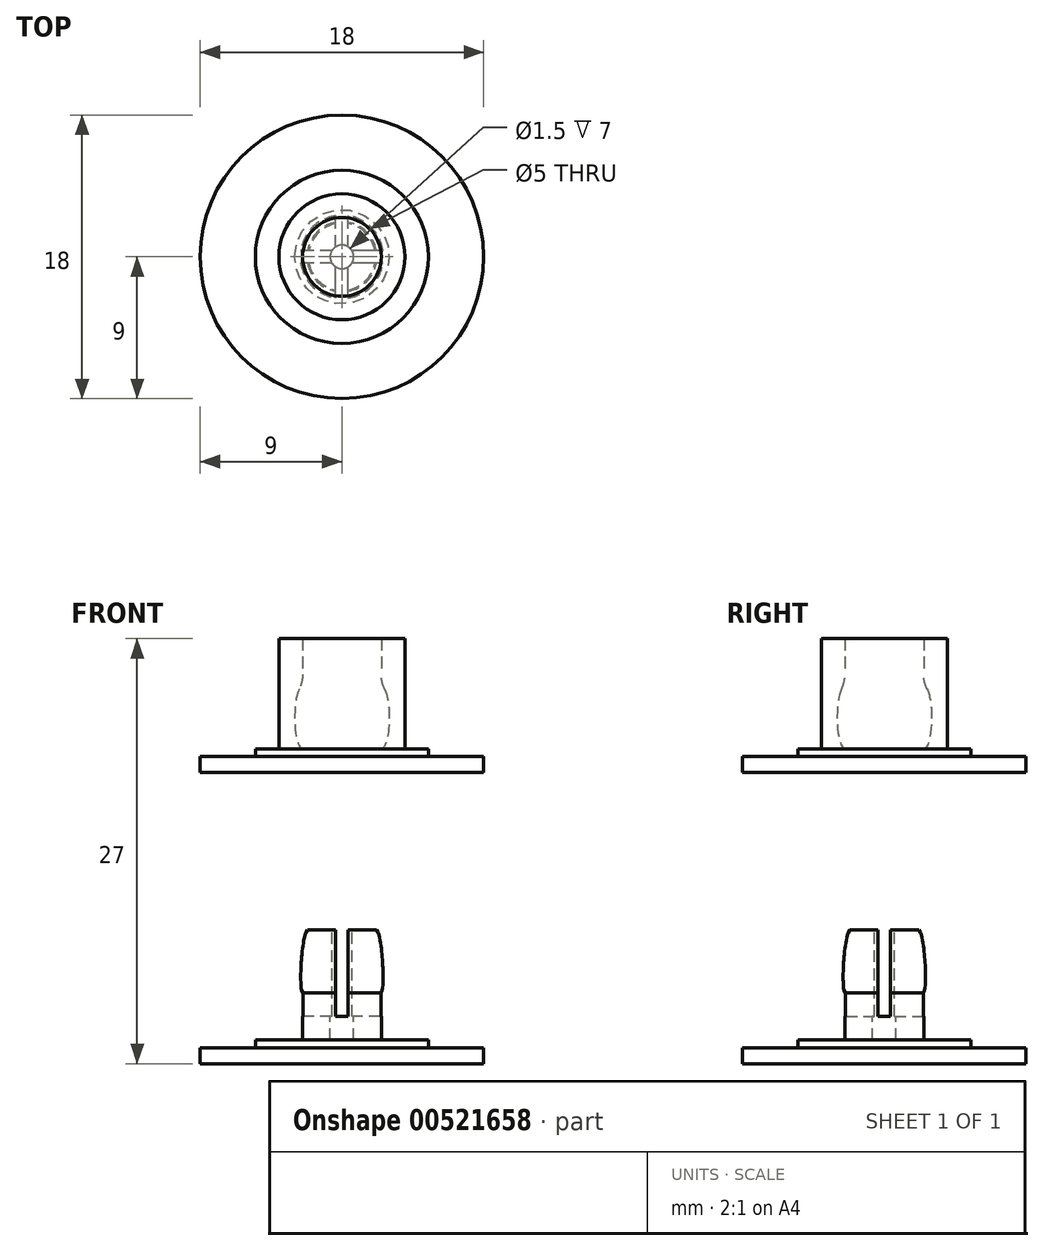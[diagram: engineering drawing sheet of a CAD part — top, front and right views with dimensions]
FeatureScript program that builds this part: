
annotation { "Feature Type Name" : "Feature", "Feature Type Description" : "" }
export const myFeature = defineFeature(function(context is Context, id is Id, definition is map)
    precondition{}
    {
        {
            var Q0;
            Q0=qCreatedBy(makeId("Front.planeOp"),FACE);
            var sketch = newSketch(context, id + "F0", { "sketchPlane" : qUnion([Q0])});
            skLineSegment(sketch, "E0", {"start": v(0, 0) * mm, "end": v(-9, 0) * mm});
            skLineSegment(sketch, "E1", {"start": v(-9, 0) * mm, "end": v(-9, 1) * mm});
            skLineSegment(sketch, "E2", {"start": v(-9, 1) * mm, "end": v(-5.5, 1) * mm});
            skLineSegment(sketch, "E3", {"start": v(-5.5, 1) * mm, "end": v(-5.5, 1.5) * mm});
            skLineSegment(sketch, "E4", {"start": v(-4, 1.5) * mm, "end": v(-5.5, 1.5) * mm});
            skLineSegment(sketch, "E5", {"start": v(-4, 1.5) * mm, "end": v(-4, 8.5) * mm});
            skLineSegment(sketch, "E6", {"start": v(-4, 8.5) * mm, "end": v(-2.5, 8.5) * mm});
            skLineSegment(sketch, "E7", {"start": v(0, -18.5) * mm, "end": v(-9, -18.5) * mm});
            skLineSegment(sketch, "E8", {"start": v(-9, -18.5) * mm, "end": v(-9, -17.5) * mm});
            skLineSegment(sketch, "E9", {"start": v(-9, -17.5) * mm, "end": v(-5.5, -17.5) * mm});
            skLineSegment(sketch, "E10", {"start": v(-5.5, -17.5) * mm, "end": v(-5.5, -17) * mm});
            skLineSegment(sketch, "E11", {"start": v(-5.5, -17) * mm, "end": v(-4, -17) * mm});
            skLineSegment(sketch, "E12", {"start": v(-2.5, -15) * mm, "end": v(-2.5, -14) * mm});
            skLineSegment(sketch, "E13", {"start": v(-2.5, 8.5) * mm, "end": v(-2.5, 5.5) * mm});
            skLineSegment(sketch, "E14", {"start": v(-2.5, 1.5) * mm, "end": v(0, 1.5) * mm});
            skLineSegment(sketch, "E15", {"start": v(0, 0) * mm, "end": v(0, 1.5) * mm});
            skEllipticalArc(sketch, "E16", {});
            skEllipticalArc(sketch, "E17", {});
            skLineSegment(sketch, "E18", {"start": v(0, -17) * mm, "end": v(-0.75, -17) * mm});
            skLineSegment(sketch, "E19", {"start": v(-0.75, -17) * mm, "end": v(-0.75, -10) * mm});
            skLineSegment(sketch, "E20", {"start": v(0, -17) * mm, "end": v(0, -18.5) * mm});
            skLineSegment(sketch, "E21", {"start": v(-2.5, -15) * mm, "end": v(-2.5, -17) * mm});
            skLineSegment(sketch, "E22", {"start": v(-4, -17) * mm, "end": v(-2.5, -17) * mm});
            skLineSegment(sketch, "E23", {"start": v(-0.75, -10) * mm, "end": v(-2.14, -10) * mm});
            skLineSegment(sketch, "E24", {"start": v(-2.14, -10) * mm, "end": v(-2.22, -10) * mm});
            const initialGuessF0  = {"E16": [-0.0023604902154368427, -0.012004871899480357, -0.06975647374412519, -0.9975640502598243, 0.002, 0.00025, 3.1415926535897936, 0], "E17": [-0.0025, 0.0035, 0, -1, 0.002, 0.0005, 3.1415926535897936, 0]};
            skSetInitialGuess(sketch, initialGuessF0);
            skSolve(sketch);
        }
        {
            var Q0;
            Q0=makeQuery(id+"F0.imprint","IMPRINT",FACE,{"disambiguationData":[TD([[makeQuery(id+"F0.imprint","IMPRINT",EDGE,{"derivedFrom":sQuery(id+"F0.wireOp",EDGE,"E0")}),-1.0]])]});
            var Q1;
            Q1=sQuery(id+"F0.wireOp",EDGE,"E15");
            revolve(context, id + "F1", {"entities" : qUnion([Q0]), "axis" : qUnion([Q1]), "revolveType" : RevolveType.ONE_DIRECTION, "angle" : 360 * degree});
        }
        {
            var Q0;
            Q0=makeQuery(id+"F1.opRevolve","SWEPT_EDGE",EDGE,{"disambiguationData":[OSD([sQuery(id+"F0.wireOp",EDGE,"E13"),sQuery(id+"F0.wireOp",EDGE,"E17")])]});
            fillet(context, id + "F2", {"entities" : qUnion([Q0]), "radius" : 2 * mm, "tangentPropagation" : true, "allowEdgeOverflow" : false});
        }
        {
            var Q0;
            Q0=makeQuery(id+"F0.imprint","IMPRINT",FACE,{"disambiguationData":[TD([[makeQuery(id+"F0.imprint","IMPRINT",EDGE,{"derivedFrom":sQuery(id+"F0.wireOp",EDGE,"E7")}),-1.0]])]});
            var Q1;
            Q1=sQuery(id+"F0.wireOp",EDGE,"E20");
            revolve(context, id + "F3", {"entities" : qUnion([Q0]), "axis" : qUnion([Q1]), "revolveType" : RevolveType.FULL});
        }
        {
            var Q0;
            Q0=makeQuery(id+"F3.opRevolve","SWEPT_FACE",FACE,{"disambiguationData":[OSD([sQuery(id+"F0.wireOp",EDGE,"E23")])]});
            var sketch = newSketch(context, id + "F4", { "sketchPlane" : qUnion([Q0])});
            skLineSegment(sketch, "E25.bottom", {"start": v(0.4, -6) * mm, "end": v(-0.4, -6) * mm});
            skLineSegment(sketch, "E25.top", {"start": v(0.4, 6) * mm, "end": v(-0.4, 6) * mm});
            skLineSegment(sketch, "E25.left", {"start": v(0.4, -6) * mm, "end": v(0.4, 6) * mm});
            skLineSegment(sketch, "E25.right", {"start": v(-0.4, -6) * mm, "end": v(-0.4, 6) * mm});
            skPoint(sketch, "E25.middle", {"position": v(0, 0) * mm});
            skLineSegment(sketch, "E26.bottom", {"start": v(6, -0.4) * mm, "end": v(-6, -0.4) * mm});
            skLineSegment(sketch, "E26.top", {"start": v(6, 0.4) * mm, "end": v(-6, 0.4) * mm});
            skLineSegment(sketch, "E26.left", {"start": v(6, -0.4) * mm, "end": v(6, 0.4) * mm});
            skLineSegment(sketch, "E26.right", {"start": v(-6, -0.4) * mm, "end": v(-6, 0.4) * mm});
            skSolve(sketch);
        }
        {
            var Q0;
            {var subQ0=sQuery(id+"F4.wireOp",EDGE,"E25.bottom");Q0=makeQuery(id+"F4.imprint","IMPRINT",FACE,{"disambiguationData":[TD([[makeQuery(id+"F4.imprint","IMPRINT",EDGE,{"derivedFrom":subQ0}),-1.0]])]});}
            var Q1;
            {var subQ0=sQuery(id+"F4.wireOp",EDGE,"E25.left");var subQ1=sQuery(id+"F0.wireOp",EDGE,"E23");var subQ2=makeQuery(id+"F3.opRevolve","SWEPT_EDGE",EDGE,{"disambiguationData":[OSD([subQ1,sQuery(id+"F0.wireOp",EDGE,"E24")])]});var subQ3=makeQuery(id+"F4.imprint","INTERSECT",VERTEX,{"disambiguationData":[OD(0.0)],"derivedFrom":[subQ2,subQ0]});Q1=makeQuery(id+"F4.imprint","IMPRINT",FACE,{"disambiguationData":[TD([[makeQuery(id+"F4.imprint","IMPRINT",EDGE,{"disambiguationData":[TD([[subQ3,-1.0]])],"derivedFrom":subQ0}),1.0]])]});}
            var Q2;
            {var subQ0=sQuery(id+"F4.wireOp",EDGE,"E26.bottom");var subQ1=sQuery(id+"F4.wireOp",EDGE,"E25.left");var subQ2=makeQuery(id+"F4.imprint","INTERSECT",VERTEX,{"derivedFrom":[subQ1,subQ0]});Q2=makeQuery(id+"F4.imprint","IMPRINT",FACE,{"disambiguationData":[TD([[makeQuery(id+"F4.imprint","IMPRINT",EDGE,{"disambiguationData":[TD([[subQ2,-1.0]])],"derivedFrom":subQ0}),1.0]])]});}
            var Q3;
            {var subQ0=sQuery(id+"F4.wireOp",EDGE,"E26.bottom");var subQ1=sQuery(id+"F4.wireOp",EDGE,"E25.right");var subQ2=makeQuery(id+"F4.imprint","INTERSECT",VERTEX,{"derivedFrom":[subQ1,subQ0]});Q3=makeQuery(id+"F4.imprint","IMPRINT",FACE,{"disambiguationData":[TD([[makeQuery(id+"F4.imprint","IMPRINT",EDGE,{"disambiguationData":[TD([[subQ2,-1.0]])],"derivedFrom":subQ1}),1.0]])]});}
            var Q4;
            {var subQ0=sQuery(id+"F4.wireOp",EDGE,"E26.right");Q4=makeQuery(id+"F4.imprint","IMPRINT",FACE,{"disambiguationData":[TD([[makeQuery(id+"F4.imprint","IMPRINT",EDGE,{"derivedFrom":subQ0}),-1.0]])]});}
            var Q5;
            {var subQ0=sQuery(id+"F4.wireOp",EDGE,"E26.bottom");var subQ1=sQuery(id+"F4.wireOp",EDGE,"E25.left");var subQ2=makeQuery(id+"F4.imprint","INTERSECT",VERTEX,{"derivedFrom":[subQ1,subQ0]});Q5=makeQuery(id+"F4.imprint","IMPRINT",FACE,{"disambiguationData":[TD([[makeQuery(id+"F4.imprint","IMPRINT",EDGE,{"disambiguationData":[TD([[subQ2,-1.0]])],"derivedFrom":subQ1}),1.0]])]});}
            var Q6;
            {var subQ0=sQuery(id+"F4.wireOp",EDGE,"E26.top");var subQ1=sQuery(id+"F4.wireOp",EDGE,"E25.left");var subQ2=makeQuery(id+"F4.imprint","INTERSECT",VERTEX,{"derivedFrom":[subQ1,subQ0]});Q6=makeQuery(id+"F4.imprint","IMPRINT",FACE,{"disambiguationData":[TD([[makeQuery(id+"F4.imprint","IMPRINT",EDGE,{"disambiguationData":[TD([[subQ2,-1.0]])],"derivedFrom":subQ0}),-1.0]])]});}
            var Q7;
            {var subQ0=sQuery(id+"F4.wireOp",EDGE,"E25.left");var subQ1=sQuery(id+"F0.wireOp",EDGE,"E23");var subQ2=makeQuery(id+"F3.opRevolve","SWEPT_EDGE",EDGE,{"disambiguationData":[OSD([subQ1,sQuery(id+"F0.wireOp",EDGE,"E24")])]});var subQ3=makeQuery(id+"F4.imprint","INTERSECT",VERTEX,{"disambiguationData":[OD(1.0)],"derivedFrom":[subQ2,subQ0]});Q7=makeQuery(id+"F4.imprint","IMPRINT",FACE,{"disambiguationData":[TD([[makeQuery(id+"F4.imprint","IMPRINT",EDGE,{"disambiguationData":[TD([[subQ3,1.0]])],"derivedFrom":subQ0}),1.0]])]});}
            var Q8;
            {var subQ0=sQuery(id+"F4.wireOp",EDGE,"E25.top");Q8=makeQuery(id+"F4.imprint","IMPRINT",FACE,{"disambiguationData":[TD([[makeQuery(id+"F4.imprint","IMPRINT",EDGE,{"derivedFrom":subQ0}),1.0]])]});}
            var Q9;
            {var subQ0=sQuery(id+"F4.wireOp",EDGE,"E26.bottom");var subQ1=sQuery(id+"F0.wireOp",EDGE,"E23");var subQ2=makeQuery(id+"F3.opRevolve","SWEPT_EDGE",EDGE,{"disambiguationData":[OSD([subQ1,sQuery(id+"F0.wireOp",EDGE,"E24")])]});var subQ3=makeQuery(id+"F4.imprint","INTERSECT",VERTEX,{"disambiguationData":[OD(0.0)],"derivedFrom":[subQ2,subQ0]});Q9=makeQuery(id+"F4.imprint","IMPRINT",FACE,{"disambiguationData":[TD([[makeQuery(id+"F4.imprint","IMPRINT",EDGE,{"disambiguationData":[TD([[subQ3,-1.0]])],"derivedFrom":subQ0}),-1.0]])]});}
            var Q10;
            {var subQ0=sQuery(id+"F4.wireOp",EDGE,"E26.bottom");var subQ1=sQuery(id+"F4.wireOp",EDGE,"E25.left");var subQ2=makeQuery(id+"F4.imprint","INTERSECT",VERTEX,{"derivedFrom":[subQ1,subQ0]});Q10=makeQuery(id+"F4.imprint","IMPRINT",FACE,{"disambiguationData":[TD([[makeQuery(id+"F4.imprint","IMPRINT",EDGE,{"disambiguationData":[TD([[subQ2,-1.0]])],"derivedFrom":subQ1}),-1.0]])]});}
            var Q11;
            {var subQ0=sQuery(id+"F4.wireOp",EDGE,"E26.left");Q11=makeQuery(id+"F4.imprint","IMPRINT",FACE,{"disambiguationData":[TD([[makeQuery(id+"F4.imprint","IMPRINT",EDGE,{"derivedFrom":subQ0}),1.0]])]});}
            var Q12;
            {var subQ0=sQuery(id+"F4.wireOp",EDGE,"E26.bottom");var subQ1=sQuery(id+"F0.wireOp",EDGE,"E23");var subQ2=makeQuery(id+"F3.opRevolve","SWEPT_EDGE",EDGE,{"disambiguationData":[OSD([subQ1,sQuery(id+"F0.wireOp",EDGE,"E24")])]});var subQ3=makeQuery(id+"F4.imprint","INTERSECT",VERTEX,{"disambiguationData":[OD(1.0)],"derivedFrom":[subQ2,subQ0]});Q12=makeQuery(id+"F4.imprint","IMPRINT",FACE,{"disambiguationData":[TD([[makeQuery(id+"F4.imprint","IMPRINT",EDGE,{"disambiguationData":[TD([[subQ3,1.0]])],"derivedFrom":subQ0}),-1.0]])]});}
            extrude(context, id + "F5", {"entities" : qUnion([Q0, Q1, Q2, Q3, Q4, Q5, Q6, Q7, Q8, Q9, Q10, Q11, Q12]), "operationType" : NewBodyOperationType.REMOVE, "oppositeDirection" : true, "depth" : 5.5 * mm, "offsetDistance" : 25 * mm});
        }
    });
